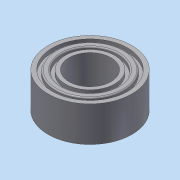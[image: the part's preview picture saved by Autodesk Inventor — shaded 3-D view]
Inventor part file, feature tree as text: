
AUTODESK INVENTOR PART (.ipt)
format: ipt  version: 2015 (Build 190159000, 159)  size: 173,568 bytes
history: native  units: mm
features: extrude x2, fillet x2, sketch x2, mirror x1
ambient origin geometry x8: Origin, YZ Plane, XZ Plane, XY Plane, X Axis, Y Axis, Z Axis, Center Point
bodies: Solid1 (feature_tree)
feature tree (7):
  extrude  "Extrusion1"  Depth=5.0mm
  extrude  "Extrusion2"  Depth=0.5mm
  fillet  "Fillet1"  Radius=0.4mm
  mirror  "Mirror1"
  fillet  "Fillet2"  Radius=0.75mm
  sketch  "Sketch1"  dims[d0=10.0mm d1=5.0mm]
  sketch  "Sketch2"  dims[d2=4.2mm d3=0.0mm d4=0.5mm d5=0.4mm d6=0.75mm d7=0.4mm d8=0.5mm d9=0.0mm d10=0.15mm d11=0.15mm]
